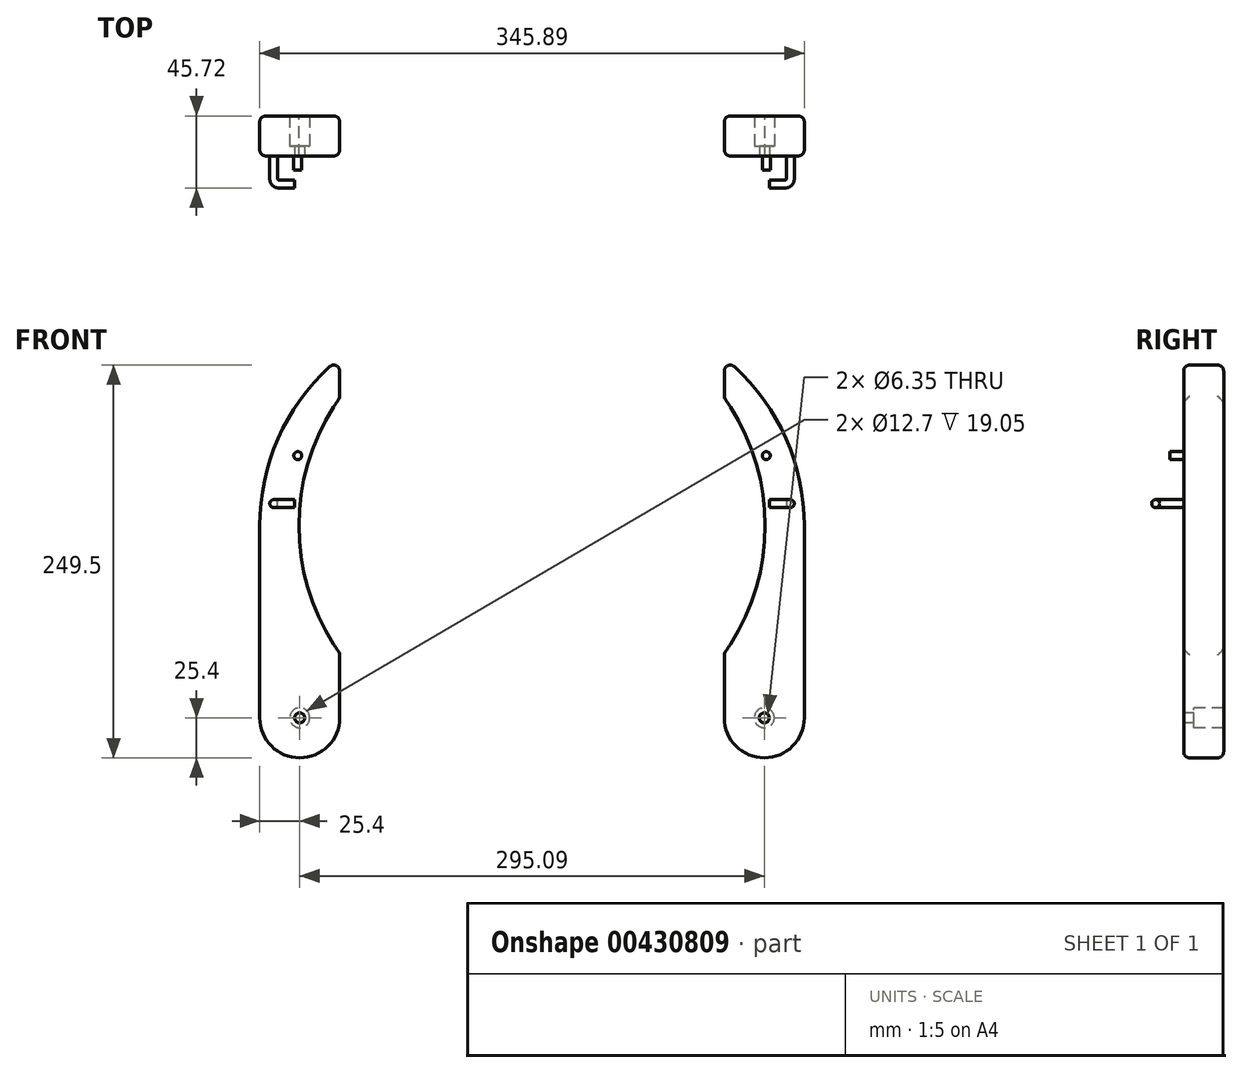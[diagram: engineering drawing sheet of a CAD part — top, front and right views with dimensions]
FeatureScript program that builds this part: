
annotation { "Feature Type Name" : "Feature", "Feature Type Description" : "" }
export const myFeature = defineFeature(function(context is Context, id is Id, definition is map)
    precondition{}
    {
        {
            var Q0;
            Q0=qCreatedBy(makeId("Front.planeOp"),FACE);
            var sketch = newSketch(context, id + "F0", { "sketchPlane" : qUnion([Q0])});
            skLineSegment(sketch, "E0.bottom", {"start": v(0, 0) * mm, "end": v(50.8, 0) * mm});
            skLineSegment(sketch, "E0.top", {"start": v(0, 254) * mm, "end": v(50.8, 254) * mm});
            skLineSegment(sketch, "E0.left", {"start": v(0, 0) * mm, "end": v(0, 254) * mm});
            skLineSegment(sketch, "E0.right", {"start": v(50.8, 0) * mm, "end": v(50.8, 254) * mm});
            skArc(sketch, "E1", {"start": v(0, 66.44) * mm, "mid": v(25.94, 147.52) * mm, "end": v(0, 228.6) * mm});
            skArc(sketch, "E2", {"start": v(0, 25.4) * mm, "mid": v(25.4, 0) * mm, "end": v(50.8, 25.4) * mm});
            skArc(sketch, "E3", {"start": v(0, 41.04) * mm, "mid": v(50.8, 147.52) * mm, "end": v(0, 254) * mm});
            skSolve(sketch);
        }
        {
            var Q0;
            {var subQ4=sQuery(id+"F0.wireOp",EDGE,"E1");Q0=makeQuery(id+"F0.imprint","IMPRINT",FACE,{"disambiguationData":[TD([[makeQuery(id+"F0.imprint","IMPRINT",EDGE,{"derivedFrom":subQ4}),-1.0]])]});}
            var Q1;
            {var subQ0=sQuery(id+"F0.wireOp",EDGE,"E2");var subQ4=sQuery(id+"F0.wireOp",EDGE,"E0.left");var subQ5=makeQuery(id+"F0.imprint","INTERSECT",VERTEX,{"derivedFrom":[subQ4,subQ0]});Q1=makeQuery(id+"F0.imprint","IMPRINT",FACE,{"disambiguationData":[TD([[makeQuery(id+"F0.imprint","IMPRINT",EDGE,{"disambiguationData":[TD([[subQ5,-1.0]])],"derivedFrom":subQ4}),-1.0]])]});}
            extrude(context, id + "F1", {"entities" : qUnion([Q0, Q1]), "depth" : 25.4 * mm});
        }
        {
            var Q0;
            Q0=makeQuery(id+"F1.opExtrude","CAP_FACE",FACE,{"disambiguationData":[OSD([sQuery(id+"F0.wireOp",EDGE,"E0.bottom"),sQuery(id+"F0.wireOp",EDGE,"E0.top"),sQuery(id+"F0.wireOp",EDGE,"E0.left"),sQuery(id+"F0.wireOp",EDGE,"E0.right"),sQuery(id+"F0.wireOp",EDGE,"E1")])],"isStart":false});
            var sketch = newSketch(context, id + "F2", { "sketchPlane" : qUnion([Q0])});
            skCircle(sketch, "E4", {"center": v(25.4, 25.4) * mm, "radius": 3.18 * mm});
            skPoint(sketch, "E4.centerSnap0", {"position": v(25.4, 0) * mm});
            skSolve(sketch);
        }
        {
            var Q0;
            Q0=makeQuery(id+"F2.imprint","IMPRINT",FACE,{"disambiguationData":[TD([[makeQuery(id+"F2.imprint","IMPRINT",EDGE,{"derivedFrom":sQuery(id+"F2.wireOp",EDGE,"E4")}),1.0]])]});
            extrude(context, id + "F3", {"entities" : qUnion([Q0]), "operationType" : NewBodyOperationType.REMOVE, "oppositeDirection" : true, "depth" : 6.35 * mm});
        }
        {
            var Q0;
            {var subQ0=sQuery(id+"F0.wireOp",EDGE,"E0.left");Q0=makeQuery(id+"F1.opExtrude","SWEPT_FACE",FACE,{"disambiguationData":[OSD([subQ0]),TDD([makeQuery(id+"F0.imprint","IMPRINT",EDGE,{"disambiguationData":[TD([[makeQuery(id+"F0.imprint","INTERSECT",VERTEX,{"disambiguationData":[OD(1.0)],"derivedFrom":[subQ0,sQuery(id+"F0.wireOp",EDGE,"E1")]}),-1.0]])],"derivedFrom":subQ0})])]});}
            var Q1;
            {var subQ0=sQuery(id+"F0.wireOp",EDGE,"E0.left");Q1=makeQuery(id+"F1.opExtrude","SWEPT_FACE",FACE,{"disambiguationData":[OSD([subQ0]),TDD([makeQuery(id+"F0.imprint","IMPRINT",EDGE,{"disambiguationData":[TD([[makeQuery(id+"F0.imprint","INTERSECT",VERTEX,{"derivedFrom":[subQ0,sQuery(id+"F0.wireOp",EDGE,"E2")]}),-1.0]])],"derivedFrom":subQ0}),makeQuery(id+"F0.imprint","IMPRINT",EDGE,{"disambiguationData":[TD([[makeQuery(id+"F0.imprint","INTERSECT",VERTEX,{"disambiguationData":[OD(0.0)],"derivedFrom":[subQ0,sQuery(id+"F0.wireOp",EDGE,"E1")]}),1.0]])],"derivedFrom":subQ0})])]});}
            fillet(context, id + "F4", {"entities" : qUnion([Q0, Q1]), "radius" : 3.8 * mm, "tangentPropagation" : true, "allowEdgeOverflow" : false});
        }
        {
            var Q0;
            Q0=makeQuery(id+"F1.opExtrude","CAP_FACE",FACE,{"disambiguationData":[OSD([sQuery(id+"F0.wireOp",EDGE,"E0.left"),sQuery(id+"F0.wireOp",EDGE,"E0.right"),sQuery(id+"F0.wireOp",EDGE,"E1"),sQuery(id+"F0.wireOp",EDGE,"E2"),sQuery(id+"F0.wireOp",EDGE,"E3")])],"isStart":false});
            var sketch = newSketch(context, id + "F5", { "sketchPlane" : qUnion([Q0])});
            skCircle(sketch, "E5", {"center": v(26.63, 192) * mm, "radius": 2.54 * mm});
            skCircle(sketch, "E6", {"center": v(26.63, 192) * mm, "radius": 12.7 * mm, "construction": true});
            skCircle(sketch, "E7", {"center": v(26.63, 192) * mm, "radius": 6.35 * mm, "construction": true});
            skLineSegment(sketch, "E8", {"start": v(32.98, 192) * mm, "end": v(32.98, 161.5) * mm, "construction": true});
            skCircle(sketch, "E9", {"center": v(41.87, 161.5) * mm, "radius": 2.54 * mm});
            skSolve(sketch);
        }
        {
            var Q0;
            Q0=makeQuery(id+"F5.imprint","IMPRINT",FACE,{"disambiguationData":[TD([[makeQuery(id+"F5.imprint","IMPRINT",EDGE,{"derivedFrom":sQuery(id+"F5.wireOp",EDGE,"E5")}),1.0]])]});
            var Q1;
            Q1=makeQuery(id+"F5.imprint","IMPRINT",FACE,{"disambiguationData":[TD([[makeQuery(id+"F5.imprint","IMPRINT",EDGE,{"derivedFrom":sQuery(id+"F5.wireOp",EDGE,"E9")}),1.0]])]});
            extrude(context, id + "F6", {"entities" : qUnion([Q0, Q1]), "operationType" : NewBodyOperationType.ADD, "depth" : 8.9 * mm});
        }
        {
            var Q0;
            Q0=qCreatedBy(makeId("Top.planeOp"),FACE);
            cPlane(context, id + "F7", {"entities" : qUnion([Q0]), "cplaneType" : CPlaneType.OFFSET, "offset" : 161.5 * mm, "width" : 152.4 * mm, "height" : 152.4 * mm});
        }
        {
            var Q0;
            Q0=makeQuery(id+"F6.opExtrude","CAP_FACE",FACE,{"disambiguationData":[OSD([sQuery(id+"F5.wireOp",EDGE,"E9")])],"isStart":false});
            var sketch = newSketch(context, id + "F8", { "sketchPlane" : qUnion([Q0])});
            skCircle(sketch, "E10", {"center": v(41.87, 161.5) * mm, "radius": 2.54 * mm});
            skSolve(sketch);
        }
        {
            var Q0;
            Q0=qCreatedBy(id+"F7.planeOp",FACE);
            var sketch = newSketch(context, id + "F9", { "sketchPlane" : qUnion([Q0])});
            skLineSegment(sketch, "E11", {"start": v(41.87, -34.3) * mm, "end": v(41.87, -40.02) * mm});
            skLineSegment(sketch, "E12", {"start": v(38.7, -43.18) * mm, "end": v(28.54, -43.18) * mm});
            skPoint(sketch, "E13.visualSharp", {"position": v(41.87, -43.18) * mm});
            skArc(sketch, "E13.filletArc", {"start": v(38.7, -43.18) * mm, "mid": v(40.94, -42.25) * mm, "end": v(41.87, -40.02) * mm});
            skSolve(sketch);
        }
        {
            var Q0;
            Q0=makeQuery(id+"F8.imprint","IMPRINT",FACE,{"disambiguationData":[TD([[makeQuery(id+"F8.imprint","IMPRINT",EDGE,{"derivedFrom":sQuery(id+"F8.wireOp",EDGE,"E10")}),1.0]])]});
            var Q1;
            Q1=sQuery(id+"F9.wireOp",EDGE,"E11");
            var Q2;
            Q2=sQuery(id+"F9.wireOp",EDGE,"E13.filletArc");
            var Q3;
            Q3=sQuery(id+"F9.wireOp",EDGE,"E12");
            sweep(context, id + "F10", {"operationType" : NewBodyOperationType.ADD, "profiles" : qUnion([Q0]), "path" : qUnion([Q1, Q2, Q3])});
        }
        {
            var Q0;
            Q0=makeQuery(id+"F3.boolean.opBoolean","COPY",FACE,{"derivedFrom":makeQuery(id+"F3.opExtrude","CAP_FACE",FACE,{"disambiguationData":[OSD([sQuery(id+"F2.wireOp",EDGE,"E4")])],"isStart":false})});
            var sketch = newSketch(context, id + "F11", { "sketchPlane" : qUnion([Q0])});
            skCircle(sketch, "E14", {"center": v(25.4, 25.4) * mm, "radius": 6.35 * mm});
            skSolve(sketch);
        }
        {
            var Q0;
            Q0=qSketchRegion(id+"F11",true);
            extrude(context, id + "F12", {"entities" : qUnion([Q0]), "operationType" : NewBodyOperationType.REMOVE, "oppositeDirection" : true, "depth" : 25.4 * mm});
        }
        {
            var Q0;
            Q0=qCreatedBy(makeId("Front.planeOp"),FACE);
            var sketch = newSketch(context, id + "F13", { "sketchPlane" : qUnion([Q0])});
            skCircle(sketch, "E15", {"center": v(-122.15, 147.52) * mm, "radius": 139.7 * mm});
            skSolve(sketch);
        }
        {
            var Q0;
            Q0=sQuery(id+"F13.wireOp",VERTEX,"E15.center");
            var Q1;
            Q1=qCreatedBy(makeId("Right.planeOp"),FACE);
            cPlane(context, id + "F14", {"entities" : qUnion([Q0, Q1]), "cplaneType" : CPlaneType.PLANE_POINT, "offset" : 25.4 * mm, "width" : 152.4 * mm, "height" : 152.4 * mm});
        }
        {
            var Q0;
            Q0=makeQuery(id+"F1.opExtrude","SWEPT_BODY",BODY,{"disambiguationData":[OSD([sQuery(id+"F0.wireOp",EDGE,"E0.left"),sQuery(id+"F0.wireOp",EDGE,"E0.right"),sQuery(id+"F0.wireOp",EDGE,"E1"),sQuery(id+"F0.wireOp",EDGE,"E2"),sQuery(id+"F0.wireOp",EDGE,"E3")])]});
            var Q1;
            Q1=qCreatedBy(id+"F14.planeOp",FACE);
            mirror(context, id + "F15", {"entities" : qUnion([Q0]), "mirrorPlane" : qUnion([Q1])});
        }
    });
